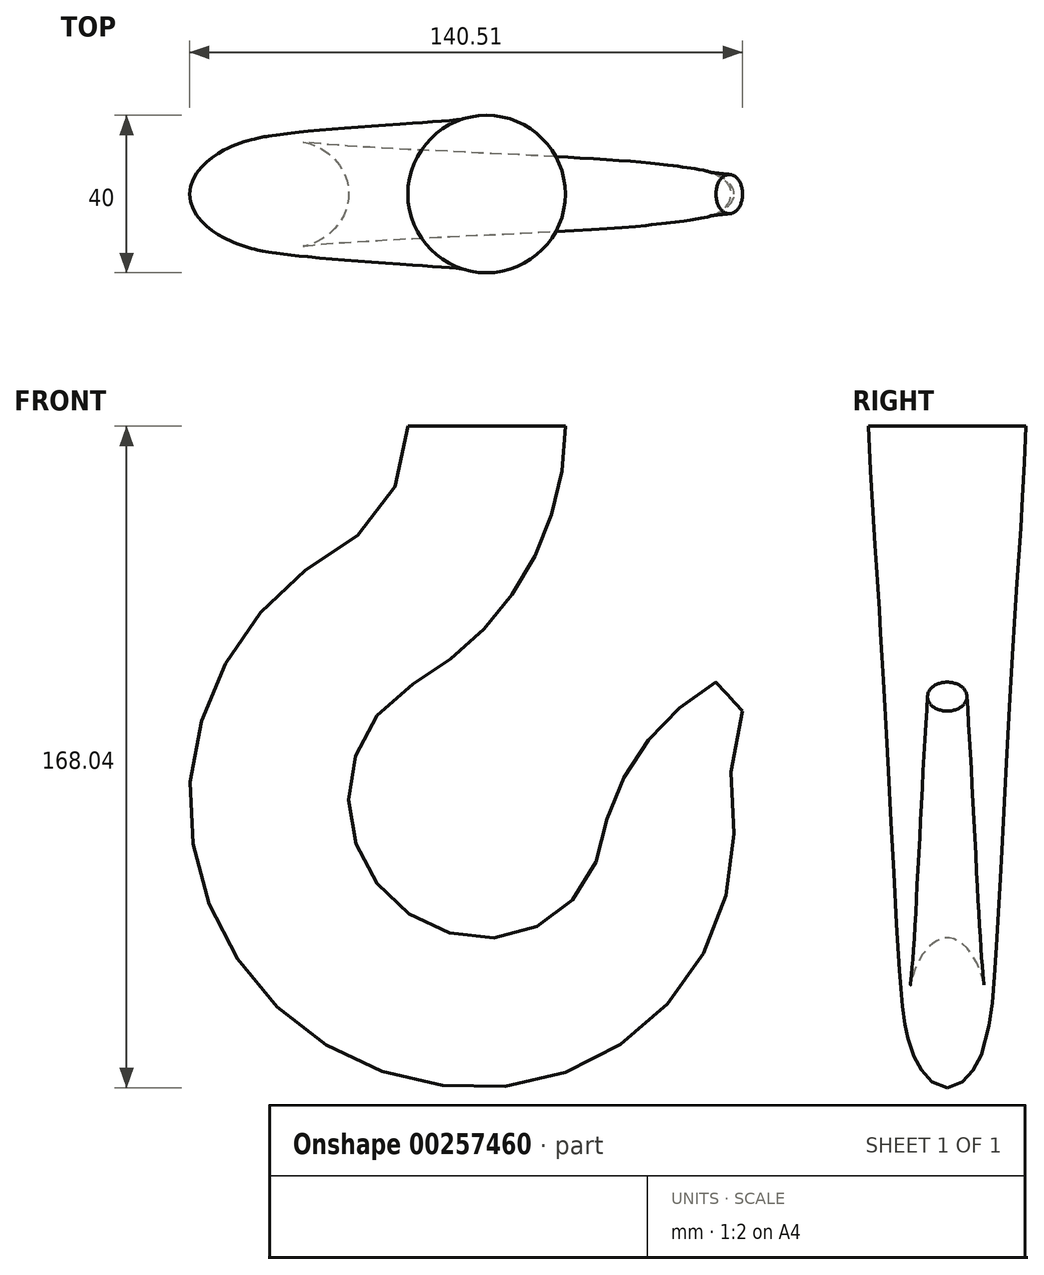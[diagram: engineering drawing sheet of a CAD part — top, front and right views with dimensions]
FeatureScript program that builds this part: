
annotation { "Feature Type Name" : "Feature", "Feature Type Description" : "" }
export const myFeature = defineFeature(function(context is Context, id is Id, definition is map)
    precondition{}
    {
        {
            var Q0;
            Q0=qCreatedBy(makeId("Front.planeOp"),FACE);
            var sketch = newSketch(context, id + "F0", { "sketchPlane" : qUnion([Q0])});
            skLineSegment(sketch, "E0", {"start": v(0, 0) * mm, "end": v(-40, 0) * mm});
            skLineSegment(sketch, "E1", {"start": v(-20, 0) * mm, "end": v(-20, -168) * mm, "construction": true});
            skLineSegment(sketch, "E2", {"start": v(-71.46, -95) * mm, "end": v(89.56, -95) * mm, "construction": true});
            skArc(sketch, "E3", {"start": v(-57.66, -31.01) * mm, "mid": v(-44.58, -17.93) * mm, "end": v(-40, 0) * mm});
            skArc(sketch, "E4", {"start": v(-37.83, -64.89) * mm, "mid": v(-10.2, -37.52) * mm, "end": v(0, 0) * mm});
            skArc(sketch, "E5", {"start": v(-57.66, -31.01) * mm, "mid": v(-84.76, -57.49) * mm, "end": v(-95.47, -93.84) * mm});
            skArc(sketch, "E6", {"start": v(-20, -168) * mm, "mid": v(27.22, -145.37) * mm, "end": v(42.43, -95.27) * mm});
            skArc(sketch, "E7", {"start": v(-55, -95) * mm, "mid": v(-44.75, -119.75) * mm, "end": v(-20, -130) * mm});
            skArc(sketch, "E8", {"start": v(9.05, -105.94) * mm, "mid": v(19.16, -82.26) * mm, "end": v(38.27, -65) * mm});
            skArc(sketch, "E9", {"start": v(42.43, -95.27) * mm, "mid": v(42.4, -83.67) * mm, "end": v(45.03, -72.36) * mm});
            skArc(sketch, "E10", {"start": v(-95.47, -93.84) * mm, "mid": v(-73.61, -147.07) * mm, "end": v(-20, -168) * mm});
            skArc(sketch, "E11", {"start": v(-37.83, -64.89) * mm, "mid": v(-50.53, -77.6) * mm, "end": v(-55, -95) * mm});
            skArc(sketch, "E12", {"start": v(-20, -130) * mm, "mid": v(-1.14, -123.2) * mm, "end": v(9.05, -105.94) * mm});
            skLineSegment(sketch, "E13", {"start": v(38.27, -65) * mm, "end": v(45.03, -72.36) * mm});
            skSolve(sketch);
        }
        {
            var Q0;
            Q0=qCreatedBy(makeId("Top.planeOp"),FACE);
            var sketch = newSketch(context, id + "F1", { "sketchPlane" : qUnion([Q0])});
            skCircle(sketch, "E14", {"center": v(-20, 0) * mm, "radius": 20 * mm});
            skPoint(sketch, "E15", {"position": v(0, 0) * mm});
            skPoint(sketch, "E16", {"position": v(-40, 0) * mm});
            skSolve(sketch);
        }
        {
            var Q0;
            Q0=sQuery(id+"F0.wireOp",EDGE,"E13");
            cPlane(context, id + "F2", {"entities" : qUnion([Q0]), "cplaneType" : CPlaneType.LINE_ANGLE, "offset" : 25 * mm, "angle" : 0 * degree, "width" : 150 * mm, "height" : 150 * mm});
        }
        {
            var Q0;
            Q0=qCreatedBy(id+"F2.planeOp",FACE);
            var sketch = newSketch(context, id + "F3", { "sketchPlane" : qUnion([Q0])});
            skCircle(sketch, "E17", {"center": v(0, -78.75) * mm, "radius": 5 * mm});
            skPoint(sketch, "E18", {"position": v(0, -73.75) * mm});
            skPoint(sketch, "E19", {"position": v(0, -83.75) * mm});
            skSolve(sketch);
        }
        {
            var Q0;
            Q0=qCreatedBy(makeId("Front.planeOp"),FACE);
            var sketch = newSketch(context, id + "F4", { "sketchPlane" : qUnion([Q0])});
            skArc(sketch, "E20.0", {"start": v(-57.66, -31.01) * mm, "mid": v(-44.58, -17.93) * mm, "end": v(-40, 0) * mm});
            skArc(sketch, "E21.0", {"start": v(-57.66, -31.01) * mm, "mid": v(-84.76, -57.49) * mm, "end": v(-95.47, -93.84) * mm});
            skArc(sketch, "E22.0", {"start": v(-95.47, -93.84) * mm, "mid": v(-73.61, -147.07) * mm, "end": v(-20, -168) * mm});
            skArc(sketch, "E23.0", {"start": v(-20, -168) * mm, "mid": v(27.22, -145.37) * mm, "end": v(42.43, -95.27) * mm});
            skArc(sketch, "E24.0", {"start": v(42.43, -95.27) * mm, "mid": v(42.4, -83.67) * mm, "end": v(45.03, -72.36) * mm});
            skSolve(sketch);
        }
        {
            var Q0;
            Q0=qCreatedBy(makeId("Front.planeOp"),FACE);
            var sketch = newSketch(context, id + "F5", { "sketchPlane" : qUnion([Q0])});
            skArc(sketch, "E25.0", {"start": v(-37.83, -64.89) * mm, "mid": v(-10.2, -37.52) * mm, "end": v(0, 0) * mm});
            skArc(sketch, "E26.0", {"start": v(-37.83, -64.89) * mm, "mid": v(-50.53, -77.6) * mm, "end": v(-55, -95) * mm});
            skArc(sketch, "E27.0", {"start": v(-55, -95) * mm, "mid": v(-44.75, -119.75) * mm, "end": v(-20, -130) * mm});
            skArc(sketch, "E28.0", {"start": v(-20, -130) * mm, "mid": v(-1.14, -123.2) * mm, "end": v(9.05, -105.94) * mm});
            skArc(sketch, "E29.0", {"start": v(9.05, -105.94) * mm, "mid": v(19.16, -82.26) * mm, "end": v(38.27, -65) * mm});
            skSolve(sketch);
        }
        {
            var Q0;
            Q0=makeQuery(id+"F1.imprint","IMPRINT",FACE,{"disambiguationData":[TD([[makeQuery(id+"F1.imprint","IMPRINT",EDGE,{"derivedFrom":sQuery(id+"F1.wireOp",EDGE,"E14")}),1.0]])]});
            var Q1;
            Q1=makeQuery(id+"F3.imprint","IMPRINT",FACE,{"disambiguationData":[TD([[makeQuery(id+"F3.imprint","IMPRINT",EDGE,{"derivedFrom":sQuery(id+"F3.wireOp",EDGE,"E17")}),1.0]])]});
            var Q2;
            Q2 = qConstructionFilter(qBodyType(qCreatedBy(id + "F4" ,EDGE), BodyType.WIRE), ConstructionObject.NO);
            var Q3;
            Q3 = qConstructionFilter(qBodyType(qCreatedBy(id + "F5" ,EDGE), BodyType.WIRE), ConstructionObject.NO);
            loft(context, id + "F6", {"addGuides" : true, "sheetProfilesArray" : [{ "sheetProfileEntities" : qUnion([Q0]) }, { "sheetProfileEntities" : qUnion([Q1]) }], "guidesArray" : [{ "guideEntities" : qUnion([Q2]), "guideDerivativeType" : LoftGuideDerivativeType.DEFAULT, "guideDerivativeMagnitude" : 1 }, { "guideEntities" : qUnion([Q3]), "guideDerivativeType" : LoftGuideDerivativeType.DEFAULT, "guideDerivativeMagnitude" : 1 }]});
        }
    });
